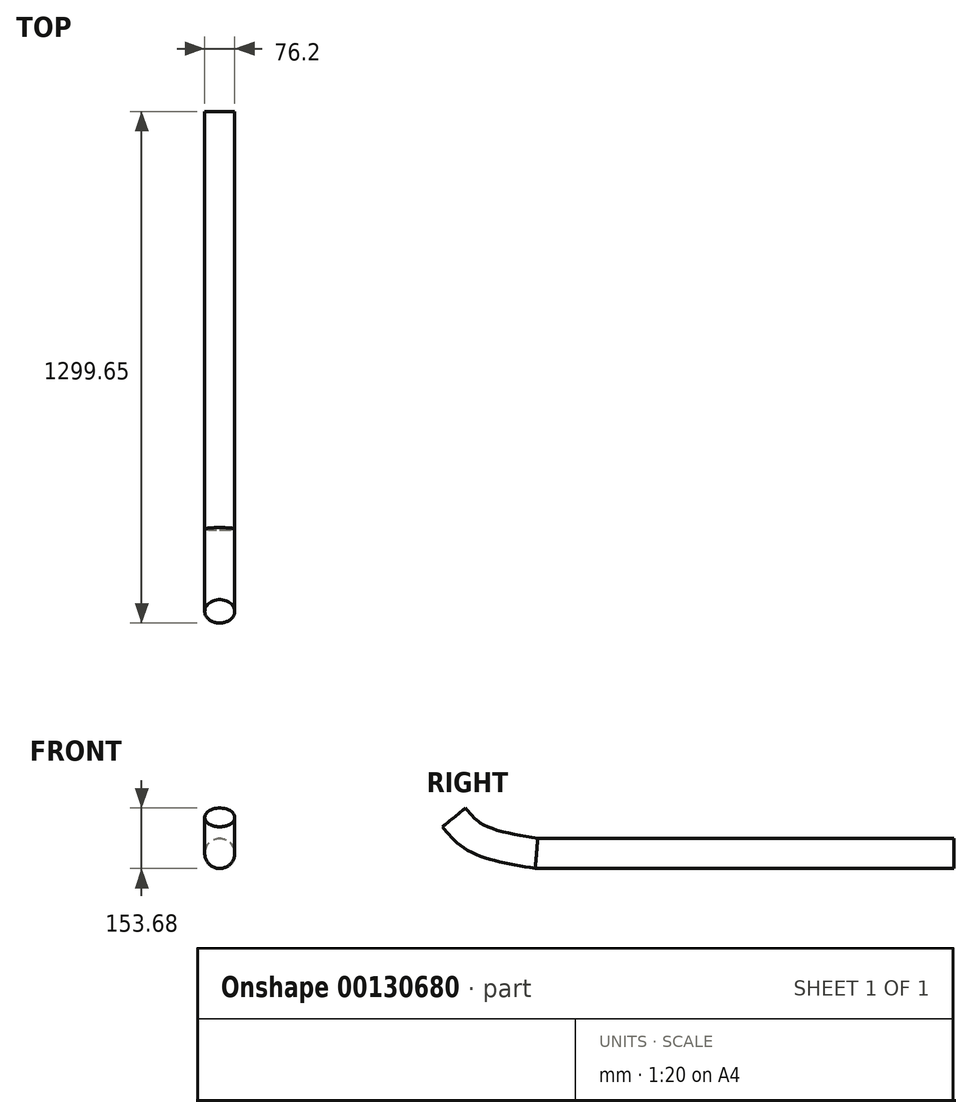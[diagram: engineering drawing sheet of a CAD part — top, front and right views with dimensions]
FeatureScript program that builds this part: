
annotation { "Feature Type Name" : "Feature", "Feature Type Description" : "" }
export const myFeature = defineFeature(function(context is Context, id is Id, definition is map)
    precondition{}
    {
        {
            var Q0;
            Q0=qCreatedBy(makeId("Front.planeOp"),FACE);
            var sketch = newSketch(context, id + "F0", { "sketchPlane" : qUnion([Q0])});
            skCircle(sketch, "E0", {"center": v(0, 0) * mm, "radius": 38.1 * mm});
            skSolve(sketch);
        }
        {
            var Q0;
            Q0=qCreatedBy(makeId("Right.planeOp"),FACE);
            var sketch = newSketch(context, id + "F1", { "sketchPlane" : qUnion([Q0])});
            skLineSegment(sketch, "E1", {"start": v(0, 0) * mm, "end": v(-1060.52, 0) * mm});
            skFitSpline(sketch, "E2", {"points": [v(-1060.52, 0) * mm, v(-1213.26, 39.28) * mm, v(-1270, 91.65) * mm], "startDerivative": vector(-295.46, 48.97) * mm, "endDerivative": vector(-112.75, 139.67) * mm});
            skSolve(sketch);
        }
        {
            var Q0;
            Q0=makeQuery(id+"F0.imprint","IMPRINT",FACE,{"disambiguationData":[TD([[makeQuery(id+"F0.imprint","IMPRINT",EDGE,{"derivedFrom":sQuery(id+"F0.wireOp",EDGE,"E0")}),1.0]])]});
            var Q1;
            Q1=sQuery(id+"F1.wireOp",EDGE,"E1");
            var Q2;
            Q2=sQuery(id+"F1.wireOp",EDGE,"E2");
            sweep(context, id + "F2", {"profiles" : qUnion([Q0]), "path" : qUnion([Q1, Q2])});
        }
    });
